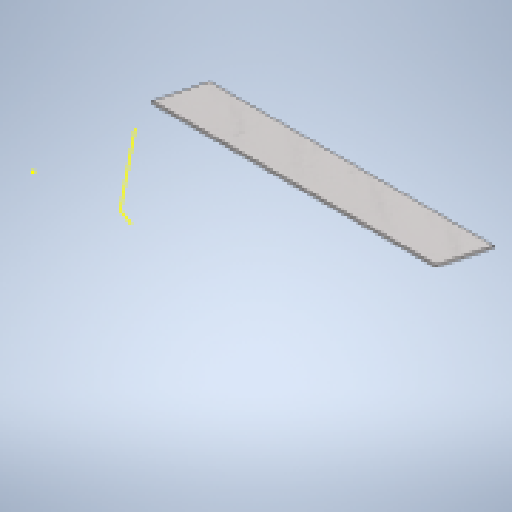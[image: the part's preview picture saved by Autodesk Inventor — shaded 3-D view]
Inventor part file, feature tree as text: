
AUTODESK INVENTOR PART (.ipt)
format: ipt  version: 2023 (Build 270158000, 158)  size: 180,736 bytes
history: native  units: mm
features: sketch x5, other x4, extrude x4, projected_geometry x3, reference x3
ambient origin geometry x8: Origin, YZ Plane, XZ Plane, XY Plane, X Axis, Y Axis, Z Axis, Center Point
bodies: Body1 (feature_tree)
feature tree (19):
  other  "Bryła1"
  extrude  "Wyciągnięcie proste1"  Depth=100.0mm
  extrude  "Wyciągnięcie proste2"  Depth=14.0mm
  extrude  "Wyciągnięcie proste3"  Depth=0.5mm TaperAngle=0.0deg
  extrude  "Wyciągnięcie proste4"  Depth=60.0mm
  sketch  "Szkic5"
  sketch  "Szkic1"
  sketch  "Szkic2"
  sketch  "Szkic3"
  projected_geometry  "Pętla rzutowana1"
  sketch  "Szkic4"
  projected_geometry  "Pętla rzutowana2"
  projected_geometry  "Pętla rzutowana3"
  reference  "Odniesienie1"
  reference  "Odniesienie2"
  reference  "Odniesienie3"
  other  "<userpath>\Desktop\MojeRoboty\Stefan\mechanics 2\STEFAN.iam"
  other  "STEFAN.iam"
  other  "uchwyt_silnikow:1"
